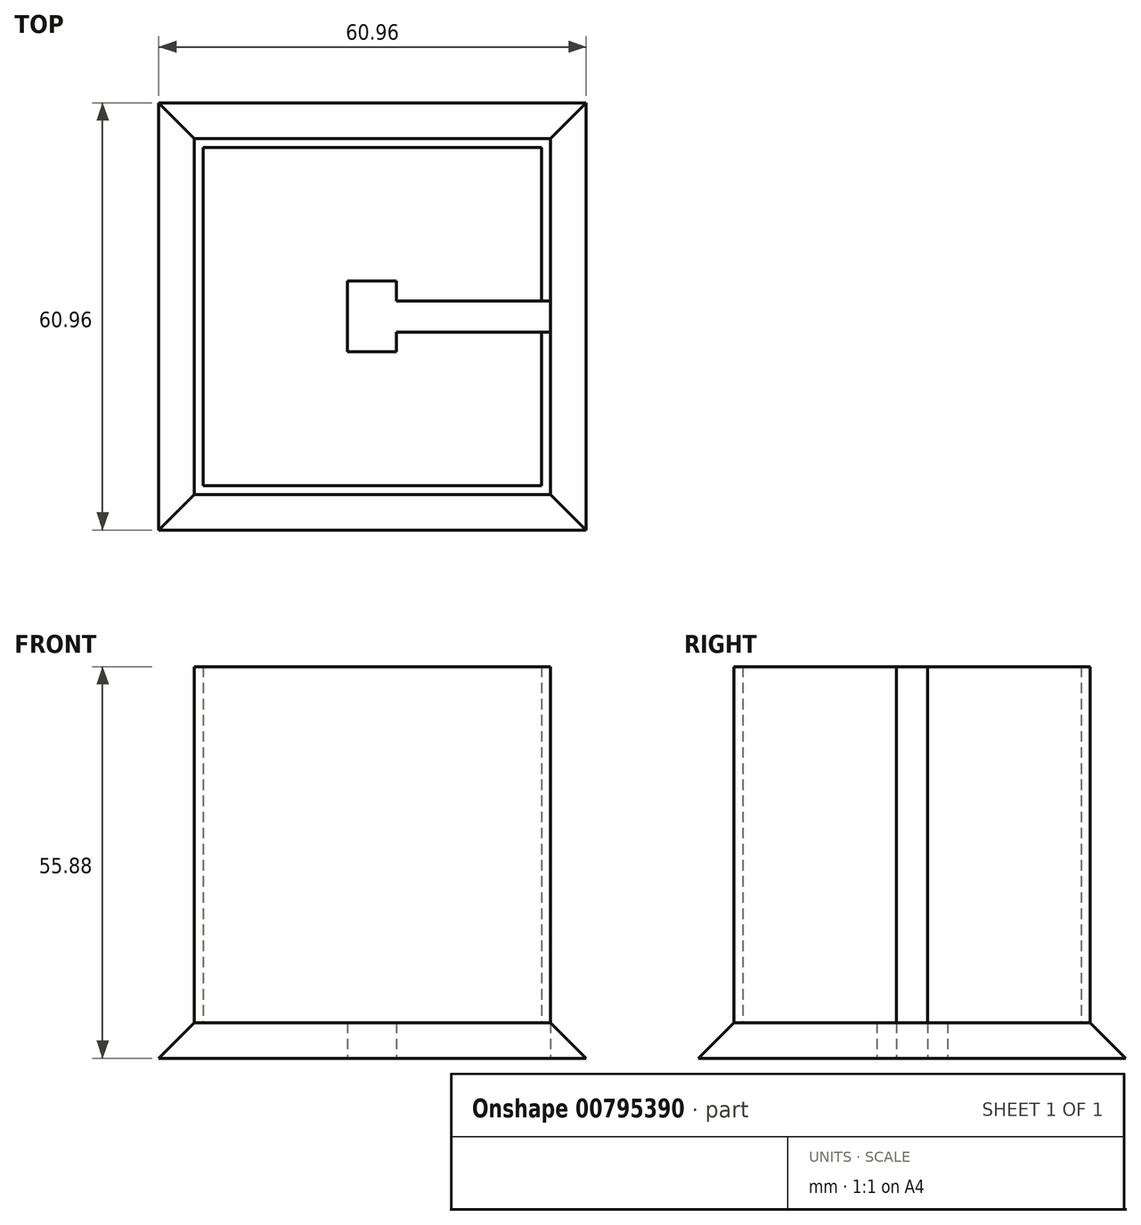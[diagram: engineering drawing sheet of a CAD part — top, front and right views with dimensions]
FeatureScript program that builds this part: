
annotation { "Feature Type Name" : "Feature", "Feature Type Description" : "" }
export const myFeature = defineFeature(function(context is Context, id is Id, definition is map)
    precondition{}
    {
        {
            var Q0;
            Q0=qCreatedBy(makeId("Top.planeOp"),FACE);
            var sketch = newSketch(context, id + "F0", { "sketchPlane" : qUnion([Q0])});
            skLineSegment(sketch, "E0.bottom", {"start": v(0, 0) * mm, "end": v(50.8, 0) * mm});
            skLineSegment(sketch, "E0.top", {"start": v(0, -50.8) * mm, "end": v(50.8, -50.8) * mm});
            skLineSegment(sketch, "E0.left", {"start": v(0, 0) * mm, "end": v(0, -50.8) * mm});
            skLineSegment(sketch, "E0.right", {"start": v(50.8, 0) * mm, "end": v(50.8, -50.8) * mm});
            skLineSegment(sketch, "E1.bottom", {"start": v(-5.08, 5.08) * mm, "end": v(55.88, 5.08) * mm});
            skLineSegment(sketch, "E1.top", {"start": v(-5.08, -55.88) * mm, "end": v(55.88, -55.88) * mm});
            skLineSegment(sketch, "E1.left", {"start": v(-5.08, 5.08) * mm, "end": v(-5.08, -55.88) * mm});
            skLineSegment(sketch, "E1.right", {"start": v(55.88, 5.08) * mm, "end": v(55.88, -55.88) * mm});
            skLineSegment(sketch, "E2.bottom", {"start": v(1.27, -1.27) * mm, "end": v(49.53, -1.27) * mm});
            skLineSegment(sketch, "E2.top", {"start": v(1.27, -49.53) * mm, "end": v(49.53, -49.53) * mm});
            skLineSegment(sketch, "E2.left", {"start": v(1.27, -1.27) * mm, "end": v(1.27, -49.53) * mm});
            skLineSegment(sketch, "E2.right", {"start": v(49.53, -1.27) * mm, "end": v(49.53, -49.53) * mm});
            skCircle(sketch, "E3", {"center": v(25.4, -25.4) * mm, "radius": 2.5 * mm});
            skPoint(sketch, "E3.centerSnap0", {"position": v(55.88, -25.4) * mm});
            skPoint(sketch, "E3.centerSnap1", {"position": v(25.4, 0) * mm});
            skLineSegment(sketch, "E4.bottom", {"start": v(21.85, -20.36) * mm, "end": v(28.8, -20.36) * mm});
            skLineSegment(sketch, "E4.top", {"start": v(21.85, -30.44) * mm, "end": v(28.8, -30.44) * mm});
            skLineSegment(sketch, "E4.left", {"start": v(21.85, -20.36) * mm, "end": v(21.85, -30.44) * mm});
            skLineSegment(sketch, "E4.right", {"start": v(28.8, -20.36) * mm, "end": v(28.8, -30.44) * mm});
            skLineSegment(sketch, "E5", {"start": v(26.54, -23.18) * mm, "end": v(61.5, -23.18) * mm});
            skLineSegment(sketch, "E6", {"start": v(26.54, -27.62) * mm, "end": v(61.5, -27.62) * mm});
            skSolve(sketch);
        }
        {
            var Q0;
            Q0 = qSketchRegion(id + "F0", true);
            var Q1;
            Q1=makeQuery(id+"F0.imprint","IMPRINT",FACE,{"disambiguationData":[TD([[makeQuery(id+"F0.imprint","IMPRINT",EDGE,{"derivedFrom":sQuery(id+"F0.wireOp",EDGE,"E2.bottom")}),-1.0]])]});
            var Q2;
            Q2=makeQuery(id+"F0.imprint","IMPRINT",FACE,{"disambiguationData":[TD([[makeQuery(id+"F0.imprint","IMPRINT",EDGE,{"derivedFrom":sQuery(id+"F0.wireOp",EDGE,"E0.bottom")}),-1.0]])]});
            extrude(context, id + "F1", {"entities" : qUnion([Q0, Q1, Q2]), "depth" : 5.08 * mm, "offsetDistance" : 25.4 * mm});
        }
        {
            var Q0;
            Q0=makeQuery(id+"F0.imprint","IMPRINT",FACE,{"disambiguationData":[TD([[makeQuery(id+"F0.imprint","IMPRINT",EDGE,{"derivedFrom":sQuery(id+"F0.wireOp",EDGE,"E0.bottom")}),-1.0]])]});
            extrude(context, id + "F2", {"entities" : qUnion([Q0]), "operationType" : NewBodyOperationType.ADD, "depth" : 55.88 * mm, "offsetDistance" : 25.4 * mm});
        }
        {
            var Q0;
            Q0=makeQuery(id+"F2.opExtrude","CAP_FACE",FACE,{"disambiguationData":[OSD([sQuery(id+"F0.wireOp",EDGE,"E0.bottom"),sQuery(id+"F0.wireOp",EDGE,"E0.top"),sQuery(id+"F0.wireOp",EDGE,"E0.left"),sQuery(id+"F0.wireOp",EDGE,"E0.right"),sQuery(id+"F0.wireOp",EDGE,"E2.bottom"),sQuery(id+"F0.wireOp",EDGE,"E2.top"),sQuery(id+"F0.wireOp",EDGE,"E2.left"),sQuery(id+"F0.wireOp",EDGE,"E2.right")])],"isStart":false});
            var sketch = newSketch(context, id + "F3", { "sketchPlane" : qUnion([Q0])});
            skLineSegment(sketch, "E7.bottom", {"start": v(0, 0) * mm, "end": v(50.8, 0) * mm});
            skLineSegment(sketch, "E7.top", {"start": v(0, -50.8) * mm, "end": v(50.8, -50.8) * mm});
            skLineSegment(sketch, "E7.left", {"start": v(0, 0) * mm, "end": v(0, -50.8) * mm});
            skLineSegment(sketch, "E7.right", {"start": v(50.8, 0) * mm, "end": v(50.8, -50.8) * mm});
            skSolve(sketch);
        }
        {
            var Q0;
            Q0=makeQuery(id+"F1.opExtrude","CAP_EDGE",EDGE,{"disambiguationData":[OSD([sQuery(id+"F0.wireOp",EDGE,"E1.left")])],"isStart":false});
            var Q1;
            Q1=makeQuery(id+"F1.opExtrude","CAP_EDGE",EDGE,{"disambiguationData":[OSD([sQuery(id+"F0.wireOp",EDGE,"E1.top")])],"isStart":false});
            var Q2;
            Q2=makeQuery(id+"F1.opExtrude","CAP_EDGE",EDGE,{"disambiguationData":[OSD([sQuery(id+"F0.wireOp",EDGE,"E1.right")])],"isStart":false});
            var Q3;
            Q3=makeQuery(id+"F1.opExtrude","CAP_EDGE",EDGE,{"disambiguationData":[OSD([sQuery(id+"F0.wireOp",EDGE,"E1.bottom")])],"isStart":false});
            chamfer(context, id + "F4", {"entities" : qUnion([Q0, Q1, Q2, Q3]), "width" : 5.08 * mm, "tangentPropagation" : true});
        }
    });
